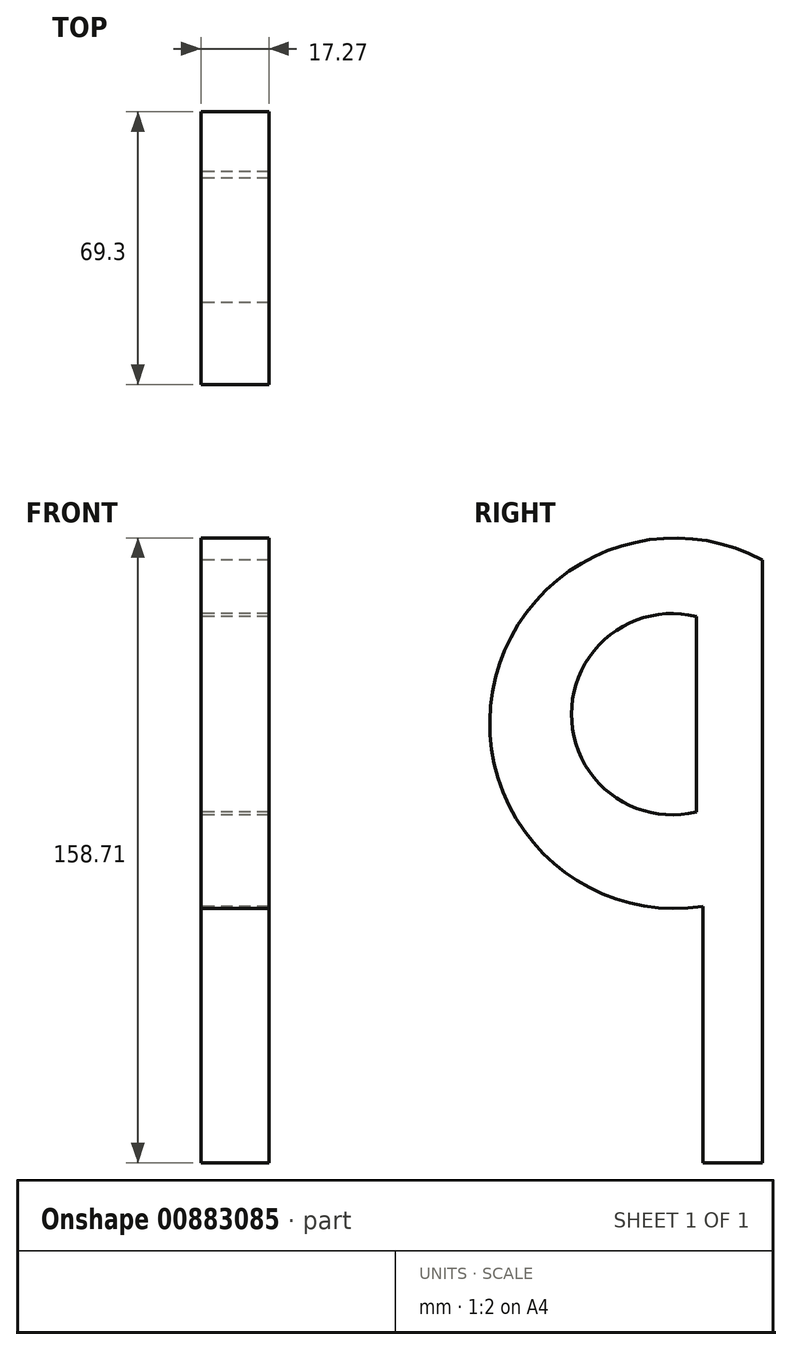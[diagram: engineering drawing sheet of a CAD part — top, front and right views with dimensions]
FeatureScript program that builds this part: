
annotation { "Feature Type Name" : "Feature", "Feature Type Description" : "" }
export const myFeature = defineFeature(function(context is Context, id is Id, definition is map)
    precondition{}
    {
        {
            var Q0;
            Q0=qCreatedBy(makeId("Right.planeOp"),FACE);
            var sketch = newSketch(context, id + "F0", { "sketchPlane" : qUnion([Q0])});
            skLineSegment(sketch, "E0", {"start": v(56.97, 76.56) * mm, "end": v(56.97, -76.56) * mm});
            skLineSegment(sketch, "E1", {"start": v(56.97, -76.56) * mm, "end": v(41.8, -76.56) * mm});
            skLineSegment(sketch, "E2", {"start": v(41.8, -76.56) * mm, "end": v(41.8, -11.45) * mm});
            skArc(sketch, "E3", {"start": v(56.97, 76.56) * mm, "mid": v(-11.65, 43.08) * mm, "end": v(41.8, -11.45) * mm});
            skLineSegment(sketch, "E4", {"start": v(40.14, 62.21) * mm, "end": v(40.14, 12.55) * mm});
            skArc(sketch, "E5", {"start": v(40.14, 62.21) * mm, "mid": v(8.45, 37.38) * mm, "end": v(40.14, 12.55) * mm});
            skSolve(sketch);
        }
        {
            var Q0;
            Q0=makeQuery(id+"F0.imprint","IMPRINT",FACE,{"disambiguationData":[TD([[makeQuery(id+"F0.imprint","IMPRINT",EDGE,{"derivedFrom":sQuery(id+"F0.wireOp",EDGE,"E0")}),-1.0]])]});
            extrude(context, id + "F1", {"entities" : qUnion([Q0]), "depth" : 17.27 * mm, "offsetDistance" : 25.4 * mm});
        }
    });
